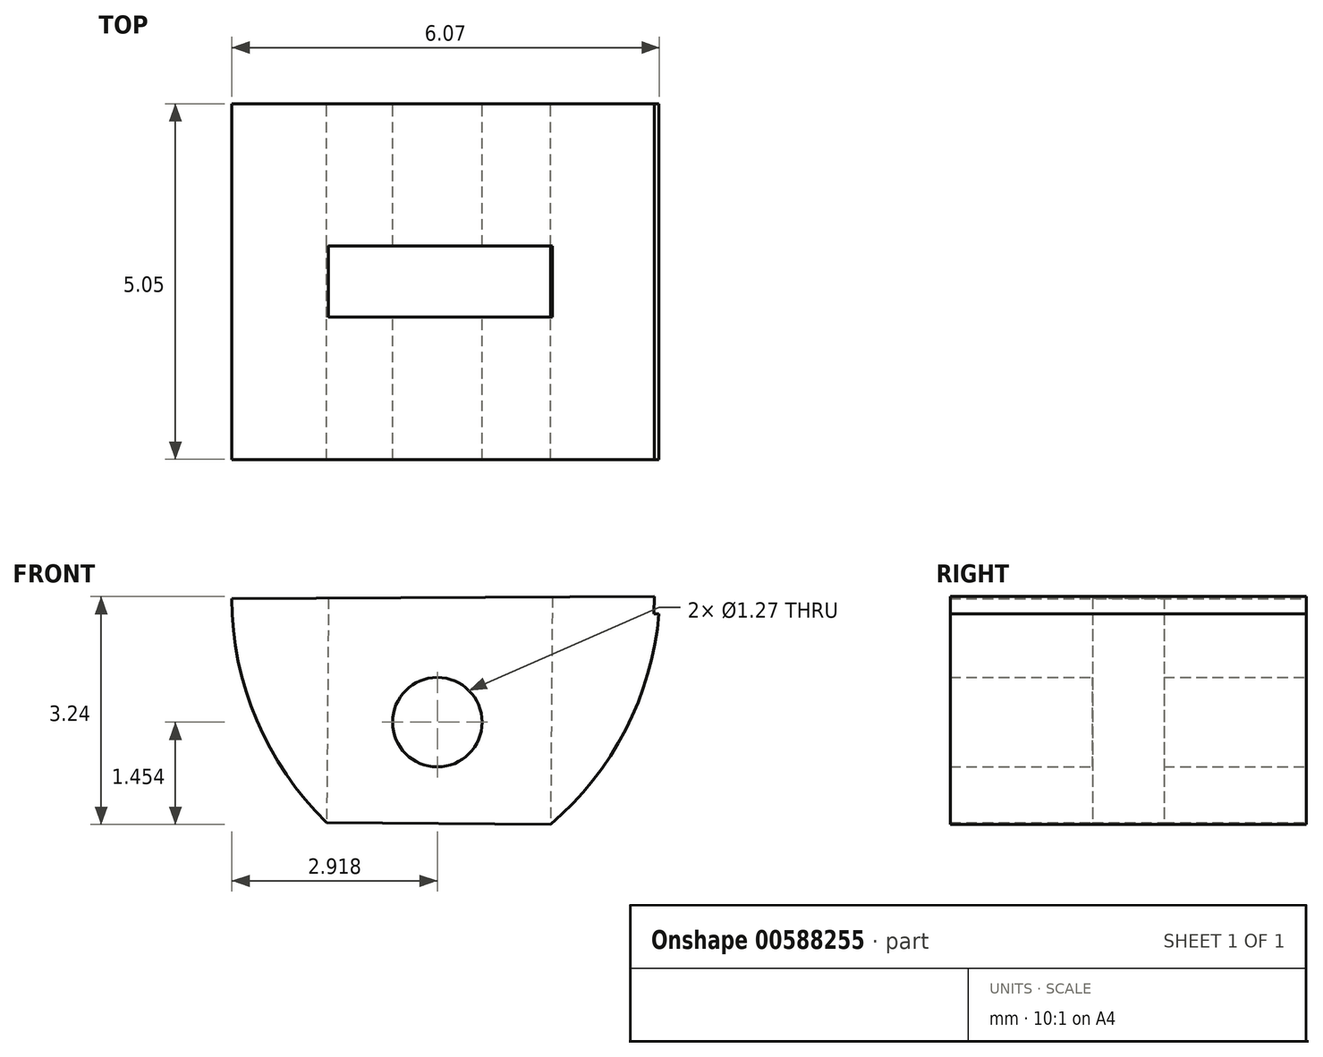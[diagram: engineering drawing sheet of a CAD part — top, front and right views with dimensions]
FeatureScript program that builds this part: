
annotation { "Feature Type Name" : "Feature", "Feature Type Description" : "" }
export const myFeature = defineFeature(function(context is Context, id is Id, definition is map)
    precondition{}
    {
        {
            var Q0;
            Q0=qCreatedBy(makeId("Front.planeOp"),FACE);
            var sketch = newSketch(context, id + "F0", { "sketchPlane" : qUnion([Q0])});
            skLineSegment(sketch, "E0", {"start": v(-51.54, 42.89) * mm, "end": v(-45.47, 42.67) * mm});
            skPoint(sketch, "E1", {"position": v(-48.62, 41.13) * mm});
            skLineSegment(sketch, "E2", {"start": v(-45.47, 42.67) * mm, "end": v(-45.55, 42.68) * mm});
            skLineSegment(sketch, "E3", {"start": v(-45.55, 42.68) * mm, "end": v(-45.54, 42.92) * mm});
            skLineSegment(sketch, "E4", {"start": v(-45.54, 42.92) * mm, "end": v(-51.54, 42.89) * mm});
            skLineSegment(sketch, "E5", {"start": v(-50.2, 39.71) * mm, "end": v(-47.01, 39.68) * mm});
            skArc(sketch, "E6", {"start": v(-47.01, 39.68) * mm, "mid": v(-45.95, 41.03) * mm, "end": v(-45.47, 42.67) * mm});
            skArc(sketch, "E7", {"start": v(-51.54, 42.89) * mm, "mid": v(-51.19, 41.16) * mm, "end": v(-50.2, 39.71) * mm});
            skSolve(sketch);
        }
        {
            var Q0;
            Q0=makeQuery(id+"F0.imprint","IMPRINT",FACE,{"disambiguationData":[TD([[makeQuery(id+"F0.imprint","IMPRINT",EDGE,{"derivedFrom":sQuery(id+"F0.wireOp",EDGE,"xew8DbxS-2CTG-lQaf-u0vu-mJmTEVqmUGcx")}),1.0]])]});
            var Q1;
            Q1=makeQuery(id+"F0.imprint","IMPRINT",FACE,{"disambiguationData":[TD([[makeQuery(id+"F0.imprint","IMPRINT",EDGE,{"derivedFrom":sQuery(id+"F0.wireOp",EDGE,"E0")}),1.0]])]});
            var Q2;
            Q2=makeQuery(id+"F0.imprint","IMPRINT",FACE,{"disambiguationData":[TD([[makeQuery(id+"F0.imprint","IMPRINT",EDGE,{"derivedFrom":sQuery(id+"F0.wireOp",EDGE,"E0")}),-1.0]])]});
            extrude(context, id + "F1", {"entities" : qUnion([Q0, Q1, Q2]), "depth" : 5.05 * mm, "offsetDistance" : 25.4 * mm});
        }
        {
            var Q0;
            Q0=sQuery(id+"F0.wireOp",VERTEX,"E1");
            var Q1;
            Q1=makeQuery(id+"F1.opExtrude","SWEPT_BODY",BODY,{"disambiguationData":[OSD([sQuery(id+"F0.wireOp",EDGE,"E2"),sQuery(id+"F0.wireOp",EDGE,"E3"),sQuery(id+"F0.wireOp",EDGE,"E4"),sQuery(id+"F0.wireOp",EDGE,"E5"),sQuery(id+"F0.wireOp",EDGE,"E6"),sQuery(id+"F0.wireOp",EDGE,"E7")])]});
            hole(context, id + "F2", {"style" : HoleStyle.SIMPLE, "endStyle" : HoleEndStyle.THROUGH, "oppositeDirection" : true, "holeDiameter" : 1.27 * mm, "majorDiameter" : 6.35 * mm, "isTappedThrough" : true, "tappedDepth" : 12.7 * mm, "tapClearance" : 3, "locations" : qUnion([Q0]), "scope" : qUnion([Q1])});
        }
        {
            var Q0;
            Q0=makeQuery(id+"F1.opExtrude","SWEPT_FACE",FACE,{"disambiguationData":[OSD([sQuery(id+"F0.wireOp",EDGE,"E5")])]});
            var sketch = newSketch(context, id + "F3", { "sketchPlane" : qUnion([Q0])});
            skLineSegment(sketch, "E8", {"start": v(-48.92, 2.02) * mm, "end": v(-47.33, 2.02) * mm});
            skLineSegment(sketch, "E9", {"start": v(-47.33, 2.02) * mm, "end": v(-47.33, 3.03) * mm});
            skLineSegment(sketch, "E10", {"start": v(-47.33, 3.03) * mm, "end": v(-50.51, 3.03) * mm});
            skLineSegment(sketch, "E11", {"start": v(-50.51, 3.03) * mm, "end": v(-50.51, 2.02) * mm});
            skLineSegment(sketch, "E12", {"start": v(-50.51, 2.02) * mm, "end": v(-48.92, 2.02) * mm});
            skSolve(sketch);
        }
        {
            var Q0;
            Q0=makeQuery(id+"F3.imprint","IMPRINT",FACE,{"disambiguationData":[TD([[makeQuery(id+"F3.imprint","IMPRINT",EDGE,{"derivedFrom":sQuery(id+"F3.wireOp",EDGE,"E8")}),1.0]])]});
            extrude(context, id + "F4", {"entities" : qUnion([Q0]), "operationType" : NewBodyOperationType.REMOVE, "oppositeDirection" : true, "depth" : 25.4 * mm, "offsetDistance" : 25.4 * mm});
        }
    });
